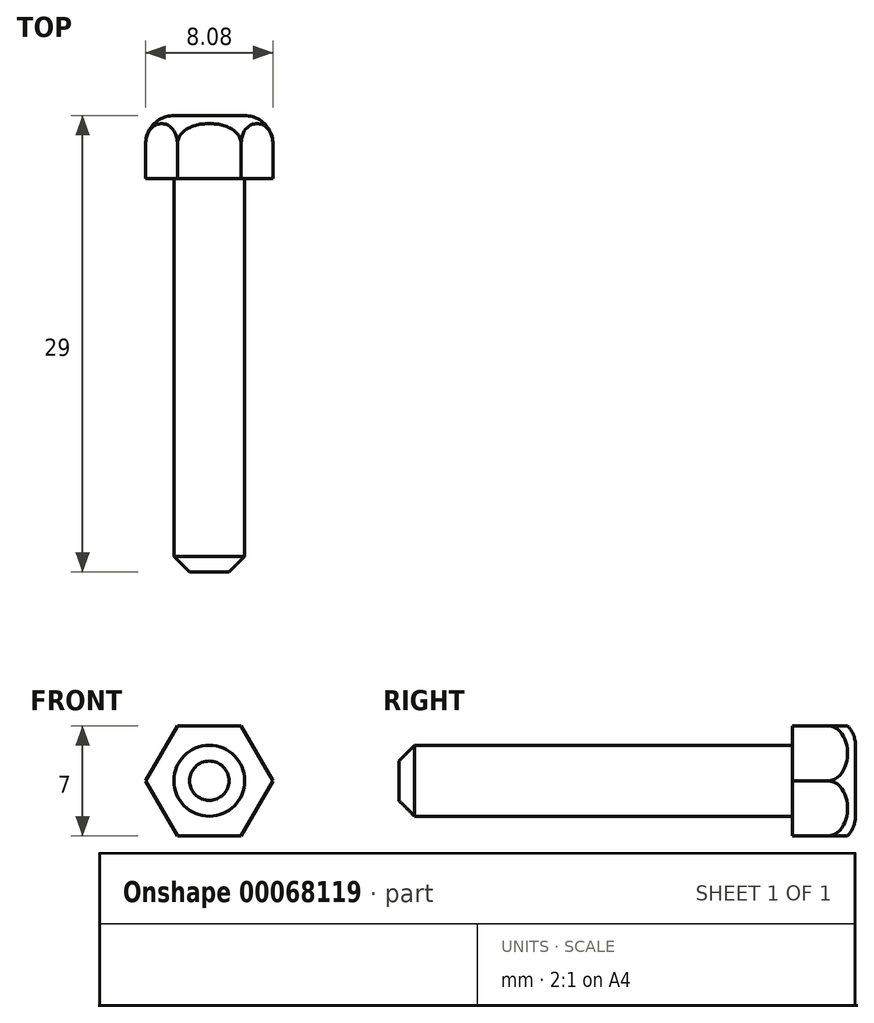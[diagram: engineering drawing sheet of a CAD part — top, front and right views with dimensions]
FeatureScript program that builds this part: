
annotation { "Feature Type Name" : "Feature", "Feature Type Description" : "" }
export const myFeature = defineFeature(function(context is Context, id is Id, definition is map)
    precondition{}
    {
        {
            var Q0;
            Q0=qCreatedBy(makeId("Front.planeOp"),FACE);
            var sketch = newSketch(context, id + "F0", { "sketchPlane" : qUnion([Q0])});
            skCircle(sketch, "E0.cCircle", {"center": v(0, 0) * mm, "radius": 3.5 * mm, "construction": true});
            skLineSegment(sketch, "E0.0", {"start": v(-2.02, 3.5) * mm, "end": v(2.02, 3.5) * mm});
            skLineSegment(sketch, "E0.1", {"start": v(2.02, 3.5) * mm, "end": v(4.04, 0) * mm});
            skLineSegment(sketch, "E0.2", {"start": v(4.04, 0) * mm, "end": v(2.02, -3.5) * mm});
            skLineSegment(sketch, "E0.3", {"start": v(2.02, -3.5) * mm, "end": v(-2.02, -3.5) * mm});
            skLineSegment(sketch, "E0.4", {"start": v(-2.02, -3.5) * mm, "end": v(-4.04, 0) * mm});
            skLineSegment(sketch, "E0.5", {"start": v(-4.04, 0) * mm, "end": v(-2.02, 3.5) * mm});
            skPoint(sketch, "E0.0.midPoint", {"position": v(0, 3.5) * mm});
            skSolve(sketch);
        }
        {
            var Q0;
            Q0=makeQuery(id+"F0.imprint","IMPRINT",FACE,{"disambiguationData":[TD([[makeQuery(id+"F0.imprint","IMPRINT",EDGE,{"derivedFrom":sQuery(id+"F0.wireOp",EDGE,"E0.0")}),-1.0]])]});
            extrude(context, id + "F1", {"entities" : qUnion([Q0]), "depth" : 4 * mm});
        }
        {
            var Q0;
            Q0=makeQuery(id+"F1.opExtrude","CAP_FACE",FACE,{"disambiguationData":[OSD([sQuery(id+"F0.wireOp",EDGE,"E0.0"),sQuery(id+"F0.wireOp",EDGE,"E0.1"),sQuery(id+"F0.wireOp",EDGE,"E0.2"),sQuery(id+"F0.wireOp",EDGE,"E0.3"),sQuery(id+"F0.wireOp",EDGE,"E0.4"),sQuery(id+"F0.wireOp",EDGE,"E0.5")])],"isStart":false});
            var sketch = newSketch(context, id + "F2", { "sketchPlane" : qUnion([Q0])});
            skCircle(sketch, "E1", {"center": v(0, 0) * mm, "radius": 2.25 * mm});
            skSolve(sketch);
        }
        {
            var Q0;
            Q0=makeQuery(id+"F2.imprint","IMPRINT",FACE,{"disambiguationData":[TD([[makeQuery(id+"F2.imprint","IMPRINT",EDGE,{"derivedFrom":sQuery(id+"F2.wireOp",EDGE,"E1")}),1.0]])]});
            extrude(context, id + "F3", {"entities" : qUnion([Q0]), "operationType" : NewBodyOperationType.ADD, "depth" : 25 * mm});
        }
        {
            var Q0;
            Q0=qCreatedBy(makeId("Top.planeOp"),FACE);
            var sketch = newSketch(context, id + "F4", { "sketchPlane" : qUnion([Q0])});
            skLineSegment(sketch, "E2", {"start": v(-4.04, -3.98) * mm, "end": v(-4.04, -1.8) * mm});
            skLineSegment(sketch, "E3", {"start": v(-2.25, 0) * mm, "end": v(0, 0) * mm});
            skLineSegment(sketch, "E4", {"start": v(0, 0) * mm, "end": v(0, 3.4) * mm});
            skLineSegment(sketch, "E5", {"start": v(0, 3.4) * mm, "end": v(-7.63, 4.23) * mm});
            skLineSegment(sketch, "E6", {"start": v(-7.63, 4.23) * mm, "end": v(-7.24, -3.98) * mm});
            skLineSegment(sketch, "E7", {"start": v(-7.24, -3.98) * mm, "end": v(-4.04, -3.98) * mm});
            skPoint(sketch, "E8.visualSharp", {"position": v(-4.04, 0) * mm});
            skArc(sketch, "E8.filletArc", {"start": v(-2.25, 0) * mm, "mid": v(-3.52, -0.52) * mm, "end": v(-4.04, -1.8) * mm});
            skSolve(sketch);
        }
        {
            var Q0;
            Q0=makeQuery(id+"F4.imprint","IMPRINT",FACE,{"disambiguationData":[TD([[makeQuery(id+"F4.imprint","IMPRINT",EDGE,{"derivedFrom":sQuery(id+"F4.wireOp",EDGE,"E2")}),1.0]])]});
            var Q1;
            Q1=sQuery(id+"F4.wireOp",EDGE,"E4");
            revolve(context, id + "F5", {"operationType" : NewBodyOperationType.REMOVE, "entities" : qUnion([Q0]), "axis" : qUnion([Q1]), "revolveType" : RevolveType.FULL, "oppositeDirection" : true});
        }
        {
            var Q0;
            Q0=makeQuery(id+"F3.opExtrude","CAP_EDGE",EDGE,{"disambiguationData":[OSD([sQuery(id+"F2.wireOp",EDGE,"E1")])],"isStart":false});
            chamfer(context, id + "F6", {"entities" : qUnion([Q0]), "width" : 1 * mm, "tangentPropagation" : true});
        }
    });
